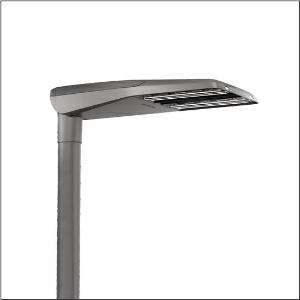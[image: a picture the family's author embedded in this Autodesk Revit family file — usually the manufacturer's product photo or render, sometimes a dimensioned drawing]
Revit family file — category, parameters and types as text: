
# Revit family: streetlight_sl_11_iq_midi___st1_2a_5xc3a41e08me_8609
name_source: partatom
category: Lighting Fixtures
units: mm (PartAtom-declared; Revit-internal decimal feet)

## family parameters
Cut with Voids When Loaded = No
Host = Face
Light Source = No
Part Type = Normal
Room Calculation Point = No
Round Connector Dimension = Use Diameter
Shared = No

## types (1)
- --- (1 x LED, 18900 lm, 124.7 W, 4000K)
    Apparent Load = 125 VA
    CIE Flux Codes = 32 70 96 100 100
    Color Rendering = 70
    Color Temperature = 4000K
    Default Elevation = 1800 mm
    Description = Streetlight SL 11 iQ midi, mast luminaire, primary light control with 3 zone facetted reflector, of plastic, silver coated, highly specular, primary optical cover: cover, of PMMA, transparent, light distribution: ST1.2a, light emission: direct distribution, primary light characteristic: asymmetric, installation type: post-top, side-entry, LED, High Power LED, rated luminous flux: 18.900lm, luminous efficacy: 152lm/W, light colour: 740, colour temperature: 4000K, control: optimised constant luminous flux control (CLO 2.0), Desk-Remote (wireless, voltage-free reading and setting of iQ features in the workshop via application-optimized NFC function/RFID function), Light-Fading, Smart-Wire, Night-Set, Lumen-Switch, Temp-Guard, Auto-Match, with cable H07RN-F 5x 1.5mm², mains connection: 230..240V, AC, 50/60Hz, connection cable pre-assembled, cable length: 12,5m, start of lifetime: 125W, end of service life: 132W, reduction: 57W, luminaire housing, of diecast aluminium, powder-coated, Siteco® metallic grey (DB 702S), please order mast flange separately, inclination adjustable without tools: 0°, 5°, 10°, 15° (post-top) | 0°, -5°, -10°, -15° (side-entry), sealing non-destructively replaceable, multi-level sealing system, length: 780mm, width: 376mm, height: 118mm, mast flange for spigot size: 42mm (side-entry): 5XC10008XM4, 60/48mm (side-entry/post-top): 5XC10108XM2, 76/60mm (side-entry/post-top): 5XC10108XM1, equipment: Power, protection rating (complete): IP66, insulation class (complete): insulation class II (safety insulation), certification: CE, ENEC, VDE, impact resistance: IK09, permissible operating ambient temperature for outdoor applications: -25..+50°C, standard-compliant lighting for roads and squares, Environmental Product Declaration (EPD) tested and certified by an independent institute, packaging unit: 1 piece

Light Distribution: ST1.2a
    Height = 118 mm
    Lamp = 1 x LED
    Lamp Light Flux = 18900 lm
    Lamp Power = 124.7 W
    Lamp count = 1
    Length = 780 mm
    Luminous efficacy = 152 lm/W
    Manufacturer = Siteco
    ModVariant = No
    Model = 5XC3A41E08ME
    Number of Poles = 1
    OnlyDefault = Yes
    Power Factor = 1
    Product Name = Streetlight SL 11 iQ midi | ST1.2a
    Product group = mast luminaire | pylon top
    ProductGroupID = 6100
    Protection Class = Protection class II
    Protection Degree = IP 66
    RLX_Detail_Level = 1
    RLX_Emergency_Light_Flux = 0 lm
    RLX_Emergency_Type = 0
    RLX_Emergency_Type_DB = No
    RlxData = <blob elided: 70749 chars, md5=db97c421>
    Socket = socket
    Standby Power = 0 W
    System Light Flux = 18900 lm
    System Power = 125 W
    Type Comments = factory setting: luminous flux: 100 % | dim-lin: 254 | 557 mA
    Type Image = l_1005960.jpg
    URL = http://relux.com
    VarID = @adj_149817
    Voltage = 0 V
    Weight = 0.00 kg
    Width = 376 mm

## geometry (parser evidence)
native form markers: Blend x4, Sweep x9
no freeform markers — native parametric forms only
